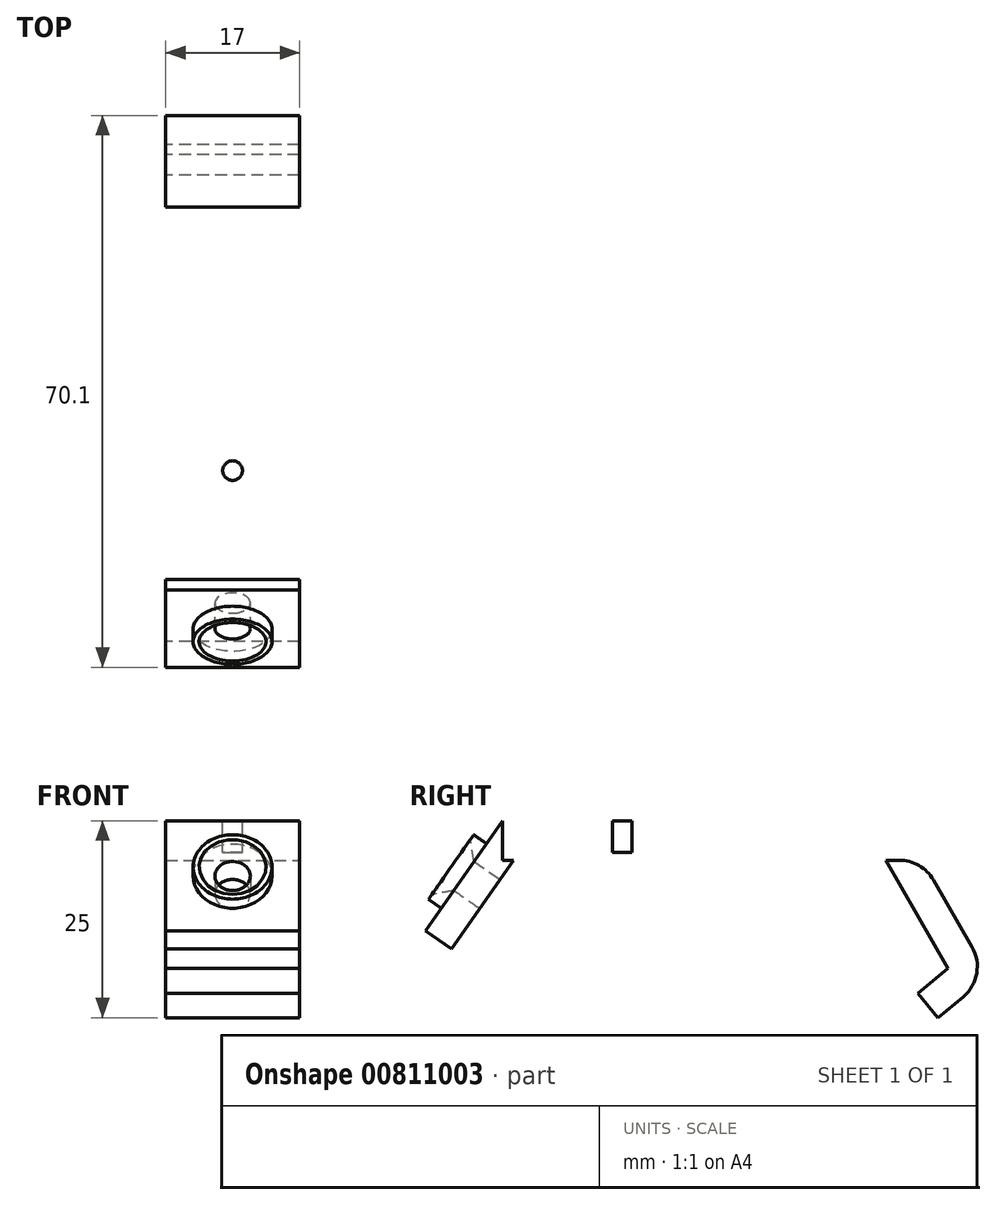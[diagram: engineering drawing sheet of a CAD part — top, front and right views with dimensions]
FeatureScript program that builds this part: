
annotation { "Feature Type Name" : "Feature", "Feature Type Description" : "" }
export const myFeature = defineFeature(function(context is Context, id is Id, definition is map)
    precondition{}
    {
        {
            var Q0;
            Q0=qCreatedBy(makeId("Right.planeOp"),FACE);
            var sketch = newSketch(context, id + "F0", { "sketchPlane" : qUnion([Q0])});
            skLineSegment(sketch, "E0", {"start": v(-23.86, -20.05) * mm, "end": v(-15.26, -7.76) * mm});
            skLineSegment(sketch, "E1", {"start": v(-15.26, -7.76) * mm, "end": v(30.74, -7.76) * mm});
            skLineSegment(sketch, "E2", {"start": v(30.74, -7.76) * mm, "end": v(39.24, -22.49) * mm});
            skLineSegment(sketch, "E3", {"start": v(39.24, -22.49) * mm, "end": v(35.41, -25.7) * mm});
            skLineSegment(sketch, "E4", {"start": v(35.41, -25.7) * mm, "end": v(37.98, -28.76) * mm});
            skLineSegment(sketch, "E5", {"start": v(37.98, -28.76) * mm, "end": v(44.39, -23.4) * mm});
            skLineSegment(sketch, "E6", {"start": v(44.39, -23.4) * mm, "end": v(33.05, -3.76) * mm});
            skLineSegment(sketch, "E7", {"start": v(33.05, -3.76) * mm, "end": v(-17.34, -3.76) * mm});
            skLineSegment(sketch, "E8", {"start": v(-17.34, -3.76) * mm, "end": v(-27.14, -17.76) * mm});
            skLineSegment(sketch, "E9", {"start": v(-27.14, -17.76) * mm, "end": v(-23.86, -20.05) * mm});
            skSolve(sketch);
        }
        {
            var Q0;
            Q0=makeQuery(id+"F0.imprint","IMPRINT",FACE,{"disambiguationData":[TD([[makeQuery(id+"F0.imprint","IMPRINT",EDGE,{"derivedFrom":sQuery(id+"F0.wireOp",EDGE,"E0")}),1.0]])]});
            extrude(context, id + "F1", {"entities" : qUnion([Q0]), "depth" : 17 * mm, "offsetDistance" : 25 * mm});
        }
        {
            var Q0;
            Q0=makeQuery(id+"F1.opExtrude","SWEPT_FACE",FACE,{"disambiguationData":[OSD([sQuery(id+"F0.wireOp",EDGE,"E8")])]});
            var sketch = newSketch(context, id + "F2", { "sketchPlane" : qUnion([Q0])});
            skLineSegment(sketch, "E10", {"start": v(0, -13.03) * mm, "end": v(17, -30.11) * mm, "construction": true});
            skLineSegment(sketch, "E11", {"start": v(17, -13.03) * mm, "end": v(0, -30.11) * mm, "construction": true});
            skCircle(sketch, "E12", {"center": v(8.5, -21.57) * mm, "radius": 2.25 * mm});
            skCircle(sketch, "E13", {"center": v(8.5, -21.57) * mm, "radius": 5 * mm});
            skSolve(sketch);
        }
        {
            var Q0;
            Q0=makeQuery(id+"F2.imprint","IMPRINT",FACE,{"disambiguationData":[TD([[makeQuery(id+"F2.imprint","IMPRINT",EDGE,{"derivedFrom":sQuery(id+"F2.wireOp",EDGE,"E12")}),-1.0]])]});
            extrude(context, id + "F3", {"entities" : qUnion([Q0]), "operationType" : NewBodyOperationType.ADD, "depth" : 2 * mm, "offsetDistance" : 25 * mm});
        }
        {
            var Q0;
            Q0=makeQuery(id+"F3.boolean.opBoolean","SPLIT",FACE,{"disambiguationData":[TD([makeQuery(id+"F3.opExtrude","SWEPT_FACE",FACE,{"disambiguationData":[OSD([sQuery(id+"F2.wireOp",EDGE,"E12")])]})])],"derivedFrom":makeQuery(id+"F1.opExtrude","SWEPT_FACE",FACE,{"disambiguationData":[OSD([sQuery(id+"F0.wireOp",EDGE,"E8")])]})});
            extrude(context, id + "F4", {"entities" : qUnion([Q0]), "operationType" : NewBodyOperationType.REMOVE, "oppositeDirection" : true, "depth" : 10 * mm, "offsetDistance" : 25 * mm});
        }
        {
            var Q0;
            Q0=makeQuery(id+"F1.opExtrude","SWEPT_FACE",FACE,{"disambiguationData":[OSD([sQuery(id+"F0.wireOp",EDGE,"E7")])]});
            var sketch = newSketch(context, id + "F5", { "sketchPlane" : qUnion([Q0])});
            skLineSegment(sketch, "E14", {"start": v(0, 33.05) * mm, "end": v(17, -17.34) * mm, "construction": true});
            skLineSegment(sketch, "E15", {"start": v(17, 33.05) * mm, "end": v(0, -17.34) * mm, "construction": true});
            skCircle(sketch, "E16", {"center": v(8.5, 7.86) * mm, "radius": 1.25 * mm});
            skLineSegment(sketch, "E17", {"start": v(8.5, 33.05) * mm, "end": v(8.5, 7.86) * mm, "construction": true});
            skLineSegment(sketch, "E18", {"start": v(0, 7.86) * mm, "end": v(17, 7.86) * mm, "construction": true});
            skLineSegment(sketch, "E19", {"start": v(0, 17.86) * mm, "end": v(17, 17.86) * mm, "construction": true});
            skCircle(sketch, "E20", {"center": v(8.5, 17.86) * mm, "radius": 1.25 * mm});
            skCircle(sketch, "E21.MirrorC", {"center": v(8.5, -2.14) * mm, "radius": 1.25 * mm});
            skSolve(sketch);
        }
        {
            var Q0;
            Q0=makeQuery(id+"F5.imprint","IMPRINT",FACE,{"disambiguationData":[TD([[makeQuery(id+"F5.imprint","IMPRINT",EDGE,{"derivedFrom":sQuery(id+"F5.wireOp",EDGE,"E16")}),1.0]])]});
            var Q1;
            Q1=makeQuery(id+"F5.imprint","IMPRINT",FACE,{"disambiguationData":[TD([[makeQuery(id+"F5.imprint","IMPRINT",EDGE,{"derivedFrom":sQuery(id+"F5.wireOp",EDGE,"E20")}),1.0]])]});
            var Q2;
            Q2=makeQuery(id+"F5.imprint","IMPRINT",FACE,{"disambiguationData":[TD([[makeQuery(id+"F5.imprint","IMPRINT",EDGE,{"derivedFrom":sQuery(id+"F5.wireOp",EDGE,"E21.MirrorC")}),-1.0]])]});
            extrude(context, id + "F6", {"entities" : qUnion([Q0, Q1, Q2]), "operationType" : NewBodyOperationType.REMOVE, "oppositeDirection" : true, "depth" : 5 * mm, "offsetDistance" : 25 * mm});
        }
        {
            var Q0;
            Q0=makeQuery(id+"F3.opExtrude","CAP_EDGE",EDGE,{"disambiguationData":[OSD([sQuery(id+"F2.wireOp",EDGE,"E13")])],"isStart":true});
            var Q1;
            Q1=makeQuery(id+"F3.opExtrude","CAP_EDGE",EDGE,{"disambiguationData":[OSD([sQuery(id+"F2.wireOp",EDGE,"E12")])],"isStart":false});
            chamfer(context, id + "F7", {"entities" : qUnion([Q0, Q1]), "width" : 2 * mm, "tangentPropagation" : true});
        }
        {
            var Q0;
            Q0=makeQuery(id+"F1.opExtrude","SWEPT_EDGE",EDGE,{"disambiguationData":[OSD([sQuery(id+"F0.wireOp",EDGE,"E7"),sQuery(id+"F0.wireOp",EDGE,"E8")])]});
            var Q1;
            Q1=makeQuery(id+"F1.opExtrude","SWEPT_EDGE",EDGE,{"disambiguationData":[OSD([sQuery(id+"F0.wireOp",EDGE,"E0"),sQuery(id+"F0.wireOp",EDGE,"E1")])]});
            var Q2;
            Q2=makeQuery(id+"F1.opExtrude","SWEPT_EDGE",EDGE,{"disambiguationData":[OSD([sQuery(id+"F0.wireOp",EDGE,"E5"),sQuery(id+"F0.wireOp",EDGE,"E6")])]});
            var Q3;
            Q3=makeQuery(id+"F1.opExtrude","SWEPT_EDGE",EDGE,{"disambiguationData":[OSD([sQuery(id+"F0.wireOp",EDGE,"E6"),sQuery(id+"F0.wireOp",EDGE,"E7")])]});
            var Q4;
            Q4=makeQuery(id+"F1.opExtrude","SWEPT_EDGE",EDGE,{"disambiguationData":[OSD([sQuery(id+"F0.wireOp",EDGE,"E1"),sQuery(id+"F0.wireOp",EDGE,"E2")])]});
            fillet(context, id + "F8", {"entities" : qUnion([Q0, Q1, Q2, Q3, Q4]), "radius" : 5 * mm, "tangentPropagation" : true, "allowEdgeOverflow" : false});
        }
    });
